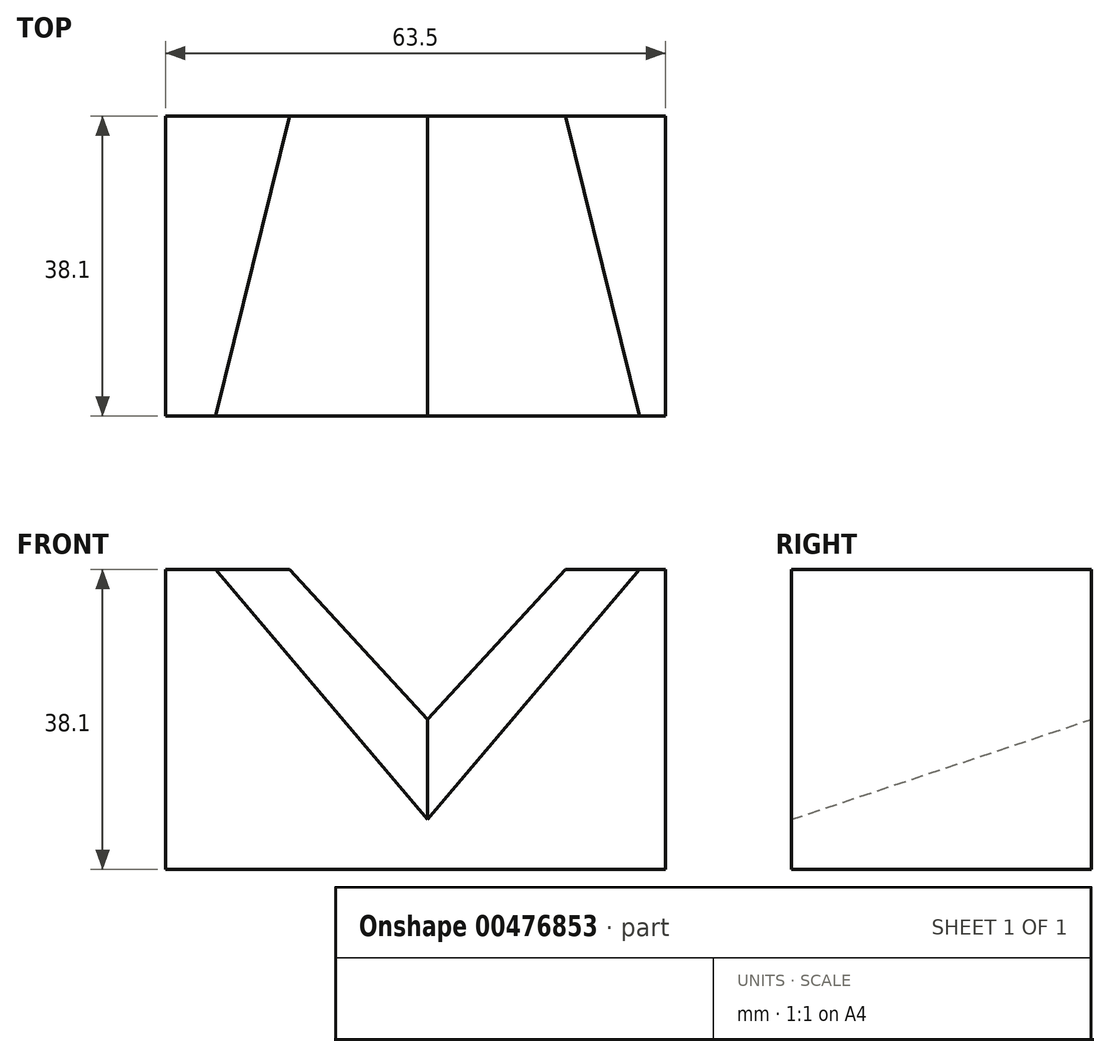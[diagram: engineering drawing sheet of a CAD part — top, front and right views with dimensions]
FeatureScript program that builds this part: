
annotation { "Feature Type Name" : "Feature", "Feature Type Description" : "" }
export const myFeature = defineFeature(function(context is Context, id is Id, definition is map)
    precondition{}
    {
        {
            var Q0;
            Q0=qCreatedBy(makeId("Front.planeOp"),FACE);
            var sketch = newSketch(context, id + "F0", { "sketchPlane" : qUnion([Q0])});
            skLineSegment(sketch, "E0", {"start": v(-33.28, 0) * mm, "end": v(30.22, 0) * mm});
            skLineSegment(sketch, "E1", {"start": v(30.22, 0) * mm, "end": v(30.22, 38.1) * mm});
            skLineSegment(sketch, "E2", {"start": v(30.22, 38.1) * mm, "end": v(-33.28, 38.1) * mm});
            skLineSegment(sketch, "E3", {"start": v(-33.28, 38.1) * mm, "end": v(-33.28, 0) * mm});
            skSolve(sketch);
        }
        {
            var Q0;
            Q0=makeQuery(id+"F0.imprint","IMPRINT",FACE,{"disambiguationData":[TD([[makeQuery(id+"F0.imprint","IMPRINT",EDGE,{"derivedFrom":sQuery(id+"F0.wireOp",EDGE,"E0")}),1.0]])]});
            extrude(context, id + "F1", {"entities" : qUnion([Q0]), "depth" : 38.1 * mm});
        }
        {
            var Q0;
            Q0=makeQuery(id+"F1.opExtrude","CAP_FACE",FACE,{"disambiguationData":[OSD([sQuery(id+"F0.wireOp",EDGE,"E0"),sQuery(id+"F0.wireOp",EDGE,"E1"),sQuery(id+"F0.wireOp",EDGE,"E2"),sQuery(id+"F0.wireOp",EDGE,"E3")])],"isStart":false});
            var sketch = newSketch(context, id + "F2", { "sketchPlane" : qUnion([Q0])});
            skLineSegment(sketch, "E4", {"start": v(-33.28, 38.1) * mm, "end": v(-26.93, 38.1) * mm, "construction": true});
            skLineSegment(sketch, "E5", {"start": v(0, 0) * mm, "end": v(0, 6.35) * mm, "construction": true});
            skLineSegment(sketch, "E6", {"start": v(-26.93, 38.1) * mm, "end": v(0, 6.35) * mm});
            skLineSegment(sketch, "E7.MirrorCS", {"start": v(26.93, 38.1) * mm, "end": v(0, 6.35) * mm});
            skSolve(sketch);
        }
        {
            var Q0;
            Q0=makeQuery(id+"F1.opExtrude","CAP_FACE",FACE,{"disambiguationData":[OSD([sQuery(id+"F0.wireOp",EDGE,"E0"),sQuery(id+"F0.wireOp",EDGE,"E1"),sQuery(id+"F0.wireOp",EDGE,"E2"),sQuery(id+"F0.wireOp",EDGE,"E3")])],"isStart":true});
            var sketch = newSketch(context, id + "F3", { "sketchPlane" : qUnion([Q0])});
            skLineSegment(sketch, "E8", {"start": v(-30.22, 38.1) * mm, "end": v(-17.52, 38.1) * mm, "construction": true});
            skLineSegment(sketch, "E9", {"start": v(0, 0) * mm, "end": v(0, 19.05) * mm, "construction": true});
            skLineSegment(sketch, "E10", {"start": v(-17.52, 38.1) * mm, "end": v(0, 19.05) * mm});
            skLineSegment(sketch, "E11.MirrorCS", {"start": v(17.52, 38.1) * mm, "end": v(0, 19.05) * mm});
            skSolve(sketch);
        }
        {
            var Q1;
            {var subQ0=sQuery(id+"F2.wireOp",EDGE,"E6");Q1=makeQuery(id+"F2.imprint","IMPRINT",FACE,{"disambiguationData":[TD([[makeQuery(id+"F2.imprint","IMPRINT",EDGE,{"derivedFrom":subQ0}),1.0]])]});}
            var Q2;
            {var subQ0=sQuery(id+"F3.wireOp",EDGE,"E10");Q2=makeQuery(id+"F3.imprint","IMPRINT",FACE,{"disambiguationData":[TD([[makeQuery(id+"F3.imprint","IMPRINT",EDGE,{"derivedFrom":subQ0}),1.0]])]});}
            loft(context, id + "F4", {"operationType" : NewBodyOperationType.REMOVE, "sheetProfilesArray" : [{ "sheetProfileEntities" : qUnion([Q1]) }, { "sheetProfileEntities" : qUnion([Q2]) }]});
        }
    });
